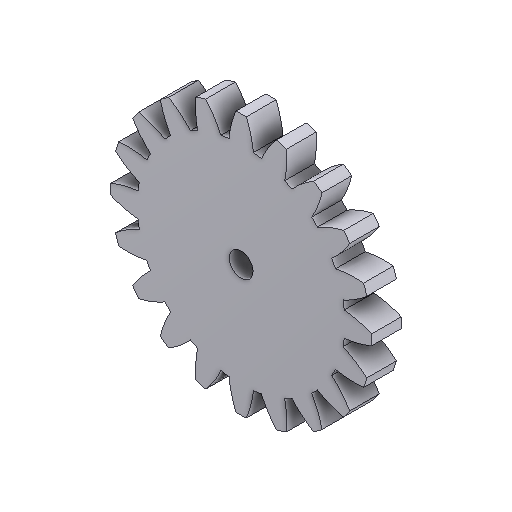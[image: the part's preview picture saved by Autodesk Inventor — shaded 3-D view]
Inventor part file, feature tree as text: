
AUTODESK INVENTOR PART (.ipt)
format: ipt  version: 2025.1 (Build 291241000, 241)  size: 314,368 bytes
history: native  units: mm
features: extrude x4, sketch x4, other x2
ambient origin geometry x8: Origin, YZ Plane, XZ Plane, XY Plane, X Axis, Y Axis, Z Axis, Center Point
bodies: Body1 (feature_tree)
feature tree (10):
  other  "Bryła1"
  extrude  "Wyciągnięcie proste1"  TaperAngle=0.0deg  [1 undecoded]
  extrude  "Wyciągnięcie proste2"  Depth=10.0mm TaperAngle=0.0deg
  extrude  "Wyciągnięcie proste3"  Depth=5.0mm TaperAngle=0.0deg
  extrude  "Wyciągnięcie proste4"  Depth=4.0mm
  sketch  "Szkic1"
  sketch  "Szkic2"
  sketch  "Szkic3"
  sketch  "Szkic4"
  other  "Gea20.stp_1_"
note: 1 required parameter value undecoded (feature->parameter linkage not recoverable at this tier; creation-order binding heuristic only, values carry confidence <= 0.55)
